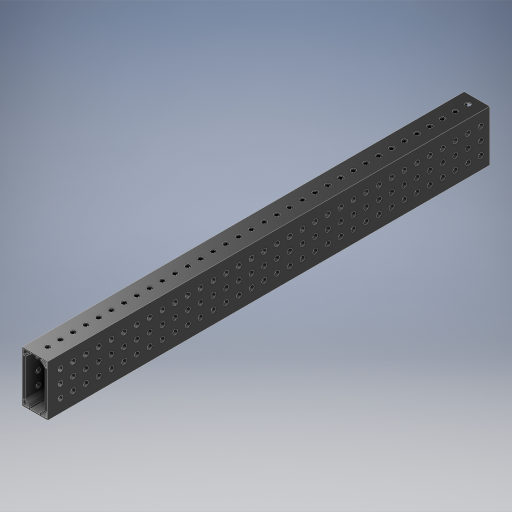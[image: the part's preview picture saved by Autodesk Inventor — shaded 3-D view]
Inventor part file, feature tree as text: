
AUTODESK INVENTOR PART (.ipt)
format: ipt  version: 2024.2 (Build 282272000, 272)  size: 1,051,648 bytes
history: native  units: in
note: dims shown in document units (in); Inventor stores cm internally (conversion verified against a paired STEP export)
features: other x13, extrude x9, hole x3, pattern_linear x3, mirror x3, sheet_metal_op x1, plane x1
ambient origin geometry x8: Origin, YZ Plane, XZ Plane, XY Plane, X Axis, Y Axis, Z Axis, Center Point
bodies: Solid1 (feature_tree)
feature tree (33):
  other  "MAXTube"
  other  "Blocks"
  other  "Base Sketch"
  extrude  "Base"  Depth=2.0in
  extrude  "MAX Corner"  Depth=1.0in
  extrude  "MAX Corner Cut"  Depth=0.125in
  extrude  "Scribe Lines"  Depth=0.04in
  other  "Side Middle"
  other  "Top Middle"
  other  "Side Holes Sketch"
  hole  "Top Side Hole"  [1 undecoded]
  hole  "Mid Side Hole"  [1 undecoded]
  hole  "Btm Side Hole"  [1 undecoded]
  pattern_linear  "Side Holes"  Spacing1=0.04in  [1 undecoded]
  mirror  "Side Mirror"
  extrude  "MAXTube Hole"  Depth=0.04in
  extrude  "MAXTube Outside"  Depth=17.346in
  pattern_linear  "MAXTube Pattern"  Spacing1=0.0in  [1 undecoded]
  mirror  "MAXTube Mirror"
  extrude  "Left Top Hole"  Depth=17.346in
  extrude  "Mid Top Hole"  TaperAngle=0.0deg  [1 undecoded]
  extrude  "Right Top Hole"  TaperAngle=0.0deg  [1 undecoded]
  pattern_linear  "Top Holes"  Spacing1=0.005in  [1 undecoded]
  mirror  "Top Mirror"
  sheet_metal_op  "Corner"
  plane  "Work Plane3"
  other  "Corner:5"
  other  "Corner:6"
  other  "Corner:7"
  other  "Corner:8"
  other  "MAXTube:1"
  other  "MAXTube:2"
  other  "MAXTube:3"
note: 8 required parameter values undecoded (feature->parameter linkage not recoverable at this tier; creation-order binding heuristic only, values carry confidence <= 0.55)
